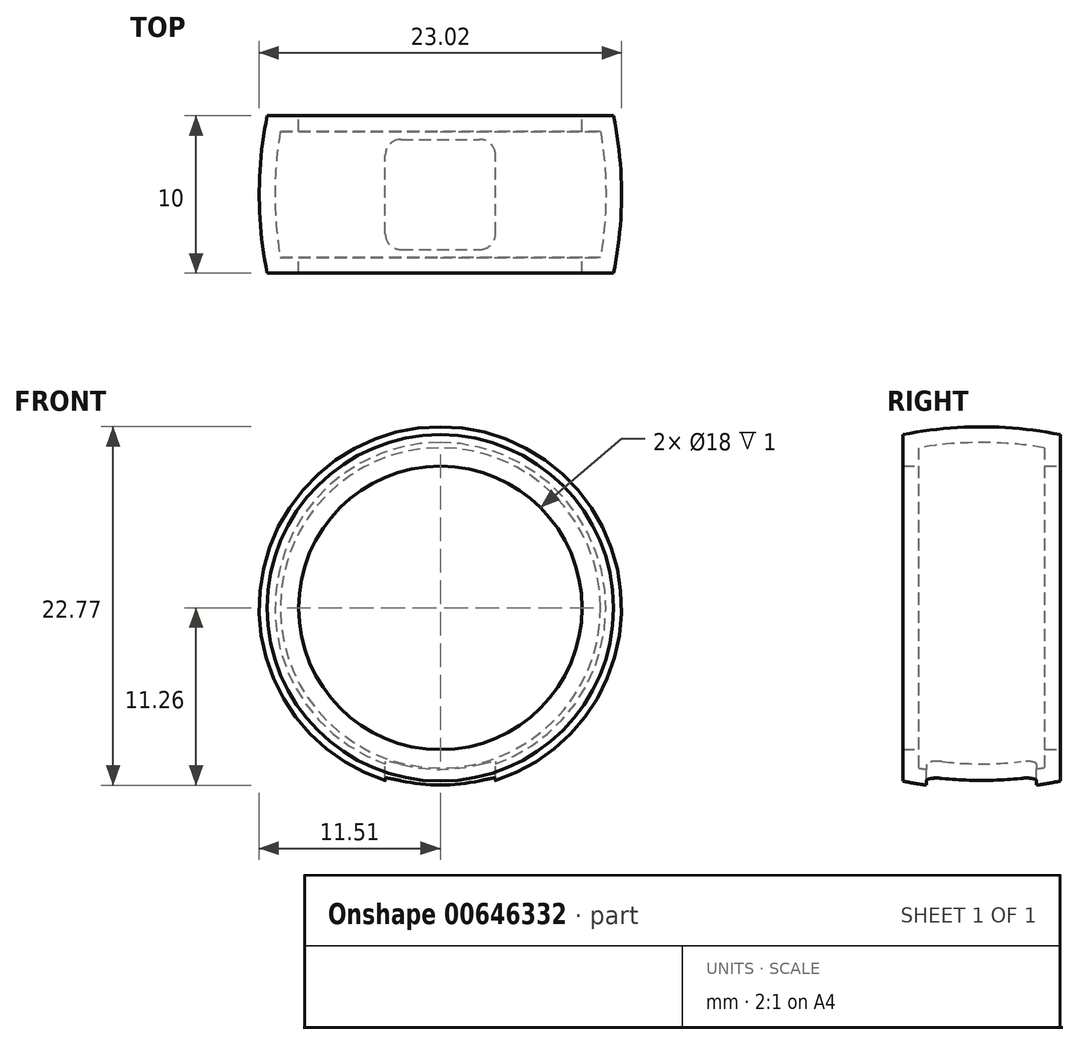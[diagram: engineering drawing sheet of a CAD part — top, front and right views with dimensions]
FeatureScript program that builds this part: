
annotation { "Feature Type Name" : "Feature", "Feature Type Description" : "" }
export const myFeature = defineFeature(function(context is Context, id is Id, definition is map)
    precondition{}
    {
        {
            var Q0;
            Q0=qCreatedBy(makeId("Top.planeOp"),FACE);
            var sketch = newSketch(context, id + "F0", { "sketchPlane" : qUnion([Q0])});
            skLineSegment(sketch, "E0", {"start": v(0, 0) * mm, "end": v(-9, 0) * mm, "construction": true});
            skLineSegment(sketch, "E1", {"start": v(-9, 5) * mm, "end": v(-9, -5) * mm});
            skLineSegment(sketch, "E2", {"start": v(-9, 5) * mm, "end": v(-11, 5) * mm});
            skLineSegment(sketch, "E3", {"start": v(-9, -5) * mm, "end": v(-11, -5) * mm});
            skArc(sketch, "E4", {"start": v(-11, 5) * mm, "mid": v(-11.5, 0) * mm, "end": v(-11, -5) * mm});
            skLineSegment(sketch, "E5", {"start": v(0, 0) * mm, "end": v(0, -10.74) * mm, "construction": true});
            skSolve(sketch);
        }
        {
            var Q0;
            Q0=makeQuery(id+"F0.imprint","IMPRINT",FACE,{"disambiguationData":[TD([[makeQuery(id+"F0.imprint","IMPRINT",EDGE,{"derivedFrom":sQuery(id+"F0.wireOp",EDGE,"E1")}),-1.0]])]});
            var Q1;
            Q1=sQuery(id+"F0.wireOp",EDGE,"E4");
            var Q2;
            Q2=sQuery(id+"F0.wireOp",EDGE,"E5");
            revolve(context, id + "F1", {"entities" : qUnion([Q0]), "surfaceEntities" : qUnion([Q1]), "axis" : qUnion([Q2]), "revolveType" : RevolveType.FULL});
        }
        {
            var Q0;
            Q0=makeQuery(id+"F1.opRevolve","SWEPT_FACE",FACE,{"disambiguationData":[OSD([sQuery(id+"F0.wireOp",EDGE,"E1")])]});
            shell(context, id + "F2", {"entities" : qUnion([Q0]), "thickness" : 1 * mm});
        }
        {
            var Q0;
            Q0=qCreatedBy(makeId("Top.planeOp"),FACE);
            var sketch = newSketch(context, id + "F3", { "sketchPlane" : qUnion([Q0])});
            skLineSegment(sketch, "E6.bottom", {"start": v(-3.5, 3.5) * mm, "end": v(3.5, 3.5) * mm});
            skLineSegment(sketch, "E6.top", {"start": v(-3.5, -3.5) * mm, "end": v(3.5, -3.5) * mm});
            skLineSegment(sketch, "E6.left", {"start": v(-3.5, 3.5) * mm, "end": v(-3.5, -3.5) * mm});
            skLineSegment(sketch, "E6.right", {"start": v(3.5, 3.5) * mm, "end": v(3.5, -3.5) * mm});
            skLineSegment(sketch, "E7", {"start": v(3.5, 3.5) * mm, "end": v(-3.5, -3.5) * mm, "construction": true});
            skSolve(sketch);
        }
        {
            var Q0;
            Q0 = qSketchRegion(id + "F3", true);
            extrude(context, id + "F4", {"entities" : qUnion([Q0]), "operationType" : NewBodyOperationType.REMOVE, "endBound" : BoundingType.THROUGH_ALL, "oppositeDirection" : true, "depth" : 25 * mm, "offsetDistance" : 25 * mm});
        }
        {
            var Q0;
            Q0=makeQuery(id+"F4.boolean.opBoolean","COPY",EDGE,{"derivedFrom":makeQuery(id+"F4.opExtrude","SWEPT_EDGE",EDGE,{"disambiguationData":[OSD([sQuery(id+"F3.wireOp",EDGE,"E6.top"),sQuery(id+"F3.wireOp",EDGE,"E6.left")])]})});
            var Q1;
            Q1=makeQuery(id+"F4.boolean.opBoolean","COPY",EDGE,{"derivedFrom":makeQuery(id+"F4.opExtrude","SWEPT_EDGE",EDGE,{"disambiguationData":[OSD([sQuery(id+"F3.wireOp",EDGE,"E6.top"),sQuery(id+"F3.wireOp",EDGE,"E6.right")])]})});
            var Q2;
            Q2=makeQuery(id+"F4.boolean.opBoolean","COPY",EDGE,{"derivedFrom":makeQuery(id+"F4.opExtrude","SWEPT_EDGE",EDGE,{"disambiguationData":[OSD([sQuery(id+"F3.wireOp",EDGE,"E6.bottom"),sQuery(id+"F3.wireOp",EDGE,"E6.right")])]})});
            var Q3;
            Q3=makeQuery(id+"F4.boolean.opBoolean","COPY",EDGE,{"derivedFrom":makeQuery(id+"F4.opExtrude","SWEPT_EDGE",EDGE,{"disambiguationData":[OSD([sQuery(id+"F3.wireOp",EDGE,"E6.bottom"),sQuery(id+"F3.wireOp",EDGE,"E6.left")])]})});
            fillet(context, id + "F5", {"entities" : qUnion([Q0, Q1, Q2, Q3]), "radius" : 1 * mm, "tangentPropagation" : true, "allowEdgeOverflow" : false});
        }
    });
